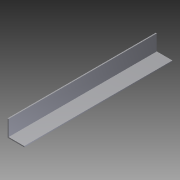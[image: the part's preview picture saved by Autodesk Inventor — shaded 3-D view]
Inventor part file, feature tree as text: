
AUTODESK INVENTOR PART (.ipt)
format: ipt  version: 2012 (Build 160160000, 160)  size: 86,528 bytes
history: native  units: in
note: dims shown in document units (in); Inventor stores cm internally (conversion verified against a paired STEP export)
features: other x3, sketch x2
ambient origin geometry x8: Origin, YZ Plane, XZ Plane, XY Plane, X Axis, Y Axis, Z Axis, Center Point
bodies: Solid1 (feature_tree)
feature tree (5):
  other  "8 ball top lift point.ipt"
  other  "Solid1::8 ball top lift point.ipt"
  sketch  "Sketch1"  dims[d0=0.3937in]
  sketch  "Sketch2"
  other  "TaggingFeature1"
